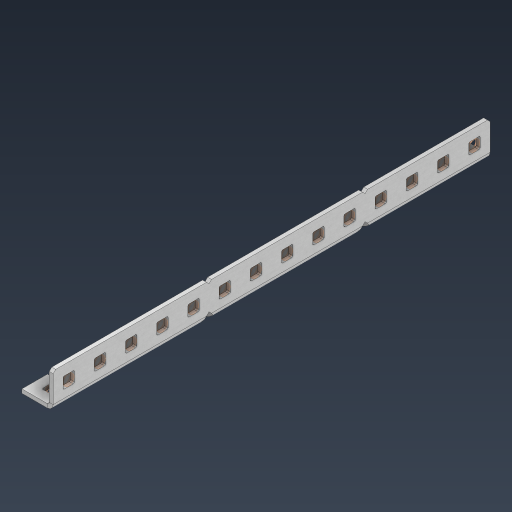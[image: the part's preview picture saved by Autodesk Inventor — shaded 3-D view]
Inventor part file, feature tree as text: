
AUTODESK INVENTOR PART (.ipt)
format: ipt  version: 2024.3 (Build 283343000, 343)  size: 696,832 bytes
history: native  units: in
note: dims shown in document units (in); Inventor stores cm internally (conversion verified against a paired STEP export)
features: other x49, extrude x40, sheet_metal_op x11, pattern_linear x2, mirror x1, chamfer x1, sketch x1
ambient origin geometry x8: Origin, YZ Plane, XZ Plane, XY Plane, X Axis, Y Axis, Z Axis, Center Point
bodies: Solid1 (feature_tree), Body (feature_tree)
feature tree (105):
  sheet_metal_op  "Flanges"
  other  "Flange Pattern Plane"
  other  "Flange Pattern Sketch"
  sheet_metal_op  "Flange Pattern"
  sheet_metal_op  "Body Pattern"
  pattern_linear  "Center Pattern"  Spacing1=7.0in  [1 undecoded]
  other  "Arc Length"
  mirror  "Notch Mirror"
  pattern_linear  "Notch Pattern"  Spacing1=0.0625in  [1 undecoded]
  chamfer  "End Chamfer"
  extrude  "Half Cut"  Depth=0.0625in
  other  "Plate1"
  sketch  "Sketch2"  dims[d0=1.0in d1=7.0in d2=0.0625in d3=0.0625in d4=0.0312in d5=0.125in d6=0.0625in d7=0.5in d8=90.0deg d9=0.0312in d10=0.25in d11=0.0625in d12=0.0625in d16=0.182in d17=0.02in d18=0.0625in d19=0.0in d20=0.25in d21=0.25in d38=5.5118in d40=0.5in d41=0.3937in d43=1.0in d46=0.172in d47=1.0in d48=0.0in d49=0.182in d50=0.02in d51=0.25in d52=0.25in d53=0.0625in d54=0.0in d55=0.172in d56=1.0in d57=0.0in d58=0.25in d60=5.5118in d62=0.5in d63=0.3937in d65=0.5in d85=0.1473in d86=0.1782in d88=0.04in d89=0.0625in d90=0.0in d91=0.04in d92=0.0491in d95=2.5in d96=0.04in d97=0.25in d98=45.0deg d99=0.25in d100=0.5in d101=0.0in d102=2.497in d106=0.182in d107=0.02in d108=0.5in d109=0.5in d110=0.0625in d111=0.0in d112=0.172in d113=0.5in d114=0.0in d117=0.5in d118=0.5in d119=0.5in]
  other  "Plate2"
  sheet_metal_op  "Bend1"
  sheet_metal_op  "Corner1"
  other  "Srf1"
  other  "Srf2"
  other  "Srf91"
  sheet_metal_op  "Body Pattern Sketch"
  other  "Srf92"
  other  "Srf786"
  other  "Srf823"
  other  "Srf824"
  other  "Srf825"
  other  "Srf826"
  other  "Srf827"
  other  "Srf828"
  other  "Srf829"
  other  "Srf856"
  other  "Srf857"
  other  "Srf858"
  other  "Srf859"
  other  "Srf860"
  other  "Srf861"
  other  "Srf862"
  other  "Srf889"
  other  "Srf890"
  other  "Srf891"
  other  "Srf892"
  other  "Srf893"
  other  "Srf894"
  other  "Srf895"
  other  "Srf896"
  other  "Srf922"
  other  "Srf923"
  other  "Srf924"
  other  "Srf925"
  other  "Srf926"
  other  "Srf959"
  other  "Srf960"
  other  "Srf961"
  other  "Srf962"
  other  "Srf963"
  other  "Srf996"
  other  "Srf997"
  other  "Srf998"
  other  "Srf999"
  other  "Srf1000"
  sheet_metal_op  "Flange Stamp"
  sheet_metal_op  "Flange Circle"
  sheet_metal_op  "Body Stamp"
  sheet_metal_op  "Body Circle"
  other  "Center Stamp"
  other  "Center Circle"
  sheet_metal_op  "Notch"
  extrude  "ExtrusionSrf2"  Depth=0.0312in
  extrude  "ExtrusionSrf92"  Depth=0.5in
  extrude  "ExtrusionSrf823"  Depth=0.0625in
  extrude  "ExtrusionSrf824"  Depth=0.5in TaperAngle=90.0deg
  extrude  "ExtrusionSrf825"  Depth=0.25in
  extrude  "ExtrusionSrf826"  Depth=0.0625in
  extrude  "ExtrusionSrf827"  Depth=0.0625in
  extrude  "ExtrusionSrf828"  Depth=0.182in
  extrude  "ExtrusionSrf829"  Depth=0.02in
  extrude  "ExtrusionSrf856"  Depth=0.0625in
  extrude  "ExtrusionSrf857"  TaperAngle=0.0deg  [1 undecoded]
  extrude  "ExtrusionSrf858"  Depth=0.25in
  extrude  "ExtrusionSrf859"  Depth=0.25in
  extrude  "ExtrusionSrf860"  Depth=0.5in
  extrude  "ExtrusionSrf861"  Depth=0.5in
  extrude  "ExtrusionSrf862"  Depth=1.0in TaperAngle=0.0deg
  extrude  "ExtrusionSrf889"  Depth=0.182in
  extrude  "ExtrusionSrf890"  Depth=0.02in
  extrude  "ExtrusionSrf891"  Depth=0.25in
  extrude  "ExtrusionSrf892"  Depth=0.25in
  extrude  "ExtrusionSrf893"  Depth=0.0625in
  extrude  "ExtrusionSrf894"  TaperAngle=0.0deg  [1 undecoded]
  extrude  "ExtrusionSrf895"  Depth=0.5in
  extrude  "ExtrusionSrf896"  Depth=1.0in TaperAngle=0.0deg
  extrude  "ExtrusionSrf922"  Depth=0.25in
  extrude  "ExtrusionSrf923"  Depth=0.5in
  extrude  "ExtrusionSrf924"  Depth=0.5in
  extrude  "ExtrusionSrf925"  Depth=0.5in
  extrude  "ExtrusionSrf926"  Depth=0.5in
  extrude  "ExtrusionSrf959"  Depth=0.5in
  extrude  "ExtrusionSrf960"  Depth=0.0625in
  extrude  "ExtrusionSrf961"  TaperAngle=0.0deg  [1 undecoded]
  extrude  "ExtrusionSrf962"  Depth=0.5in
  extrude  "ExtrusionSrf963"  Depth=0.5in
  extrude  "ExtrusionSrf996"  Depth=2.5in
  extrude  "ExtrusionSrf997"  Depth=0.25in TaperAngle=45.0deg
  extrude  "ExtrusionSrf998"  Depth=0.25in
  extrude  "ExtrusionSrf999"  Depth=0.5in TaperAngle=0.0deg
  extrude  "ExtrusionSrf1000"  Depth=0.5in
note: 5 required parameter values undecoded (feature->parameter linkage not recoverable at this tier; creation-order binding heuristic only, values carry confidence <= 0.55)
